# Revit family: Bathtub-American_Standard-Evolution-2771V_Series
name_source: partatom
category: Plumbing Fixtures
revit_build: Autodesk Revit 2014 (Build: 20130308_1515(x64)
units: mm (PartAtom-declared; Revit-internal decimal feet)

## types (9) — shared parameters
Assembly Code = D2010510
CW Connection = Yes
CWFU = 3
Default Elevation = 0"
Description = Evolution 60 Inch by 32 Inch Deep Soak Bathtub
HW Connection = Yes
HWFU = 3
Height = 21 1/2"
Installation Type = Deck Mounted
Length = 60"
Manufacturer = American Standard
Price = Prices may vary. Please consult Manufacturer Representative for most up-to-date price list.
Product Documentation Link = https://www.americanstandard-us.com
Product Page URL = https://www.americanstandard-us.com
Revised Date = 04/22/2019
URL = http://www.americanstandard-us.com
Vent Connection = No
WFU = 4
Warranty Information = 1 Year Limited
Waste Connection = Yes
Width = 32"

## per-type parameters (varying)
| type | EverClean | EverClean Combo Massage System | Finish | Material | Waste Connection Diameter | Waste Connection Radius | Water Jets |
| 2771V.418C.011 | No | Yes | Acrylic-American Standard-011-Arctic | Acrylic-American Standard-011-Arctic | 1 1/2" | 3/4" | Yes |
| 2771V.418C.020 | No | Yes | Acrylic-American Standard-020-White | Acrylic-American Standard-020-White | 2" | 1" | No |
| 2771V.418C.222 | No | Yes | Acrylic-American Standard-222-Linen | Acrylic-American Standard-222-Linen | 2" | 1" | No |
| 2771V.002.011 | No | No | Acrylic-American Standard-011-Arctic | Acrylic-American Standard-011-Arctic | 1 1/2" | 3/4" | No |
| 2771V.002.020 | No | No | Acrylic-American Standard-020-White | Acrylic-American Standard-020-White | 1 1/2" | 3/4" | No |
| 2771V.002.222 | No | No | Acrylic-American Standard-222-Linen | Acrylic-American Standard-222-Linen | 1 1/2" | 3/4" | No |
| 2771VC.011 | Yes | No | Acrylic-American Standard-011-Arctic | Acrylic-American Standard-011-Arctic | 1 1/2" | 3/4" | Yes |
| 2771VC.020 | Yes | No | Acrylic-American Standard-020-White | Acrylic-American Standard-020-White | 1 1/2" | 3/4" | Yes |
| 2771VC.222 | Yes | No | Acrylic-American Standard-222-Linen | Acrylic-American Standard-222-Linen | 1 1/2" | 3/4" | Yes |

note: column(s) folded — value = type name in every type: Model

## geometry (parser evidence)
native form markers: Sweep x1
no freeform markers — native parametric forms only
